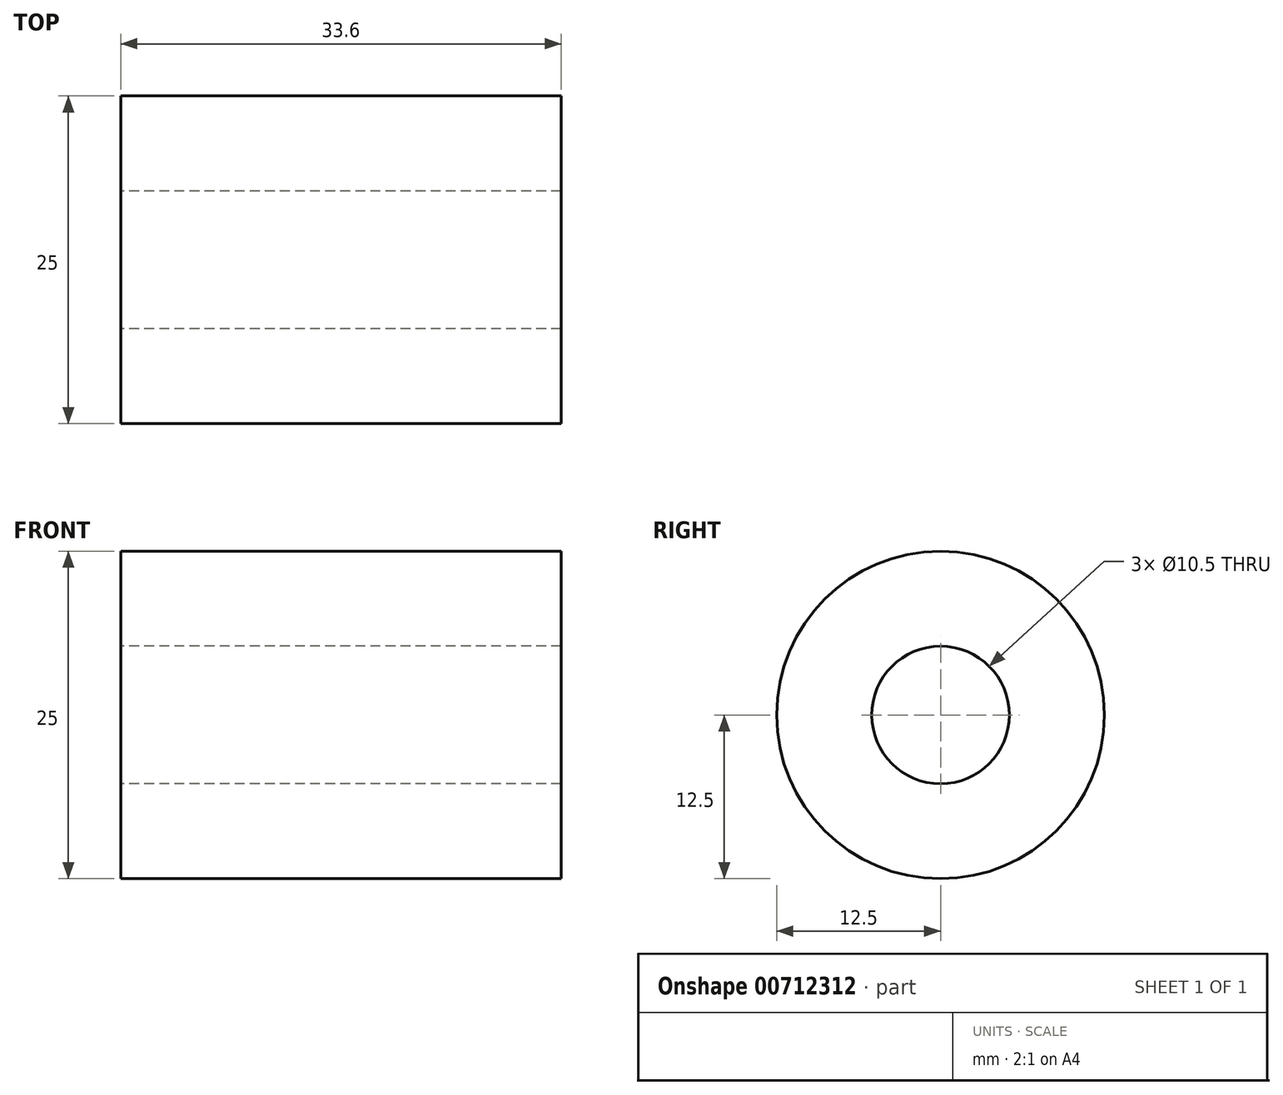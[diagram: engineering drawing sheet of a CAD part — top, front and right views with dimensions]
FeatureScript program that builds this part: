
annotation { "Feature Type Name" : "Feature", "Feature Type Description" : "" }
export const myFeature = defineFeature(function(context is Context, id is Id, definition is map)
    precondition{}
    {
        {
            var Q0;
            Q0=qCreatedBy(makeId("Right.planeOp"),FACE);
            var sketch = newSketch(context, id + "F0", { "sketchPlane" : qUnion([Q0])});
            skCircle(sketch, "E0", {"center": v(0, 0) * mm, "radius": 12.5 * mm});
            skCircle(sketch, "E1", {"center": v(0, 0) * mm, "radius": 5.25 * mm});
            skSolve(sketch);
        }
        {
            var Q0;
            Q0 = qSketchRegion(id + "F0", true);
            extrude(context, id + "F1", {"entities" : qUnion([Q0]), "depth" : 33.6 * mm, "offsetDistance" : 25 * mm});
        }
    });
